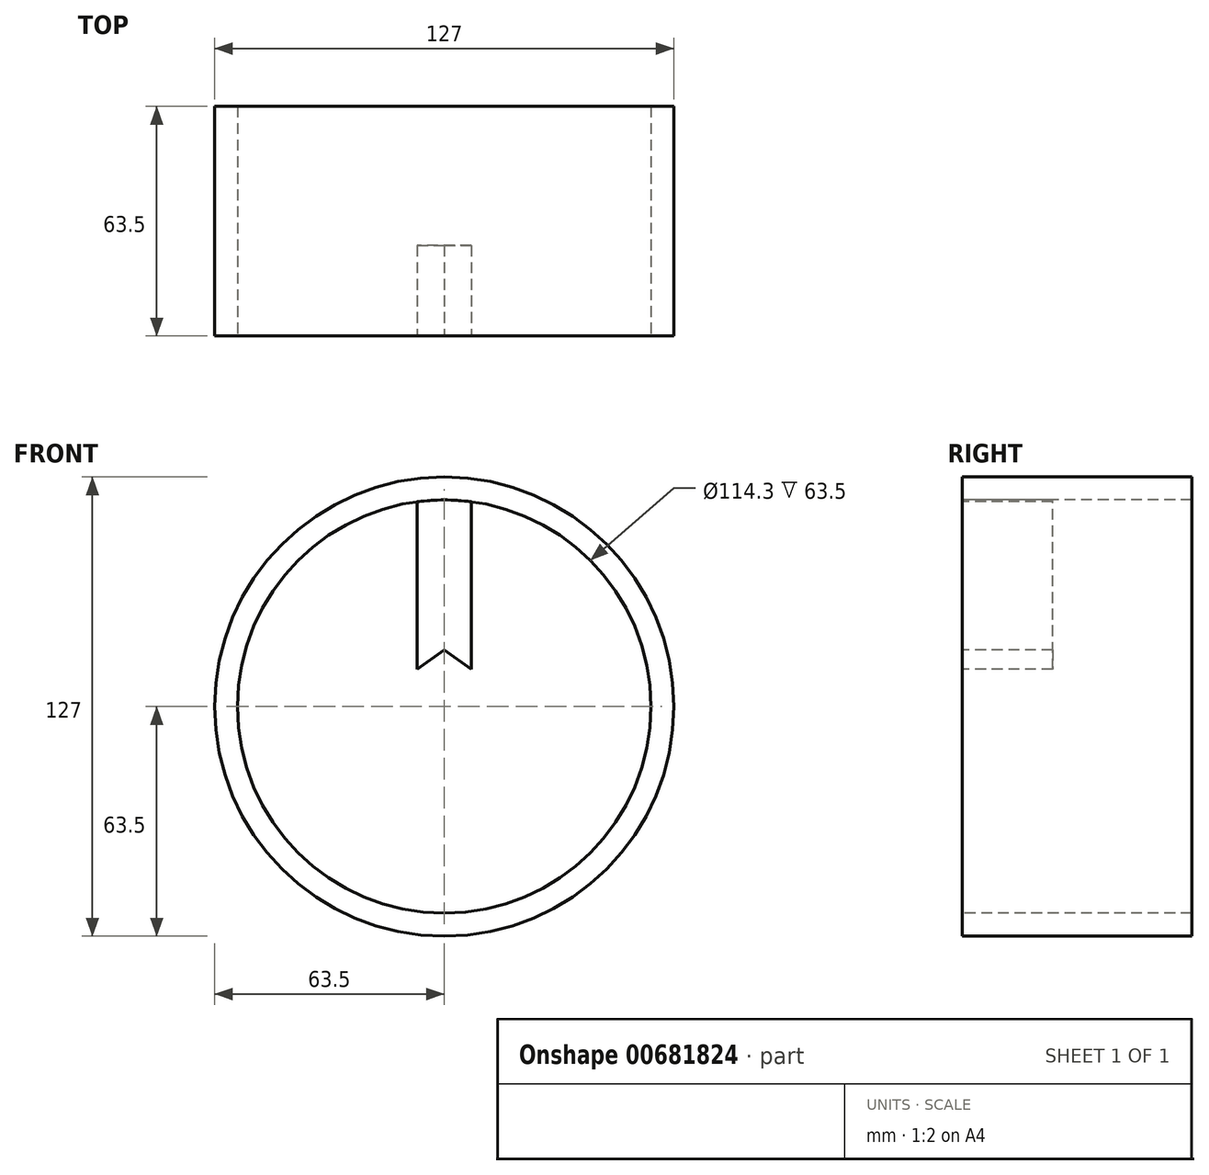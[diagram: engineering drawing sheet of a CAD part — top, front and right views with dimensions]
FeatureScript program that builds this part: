
annotation { "Feature Type Name" : "Feature", "Feature Type Description" : "" }
export const myFeature = defineFeature(function(context is Context, id is Id, definition is map)
    precondition{}
    {
        {
            var Q0;
            Q0=qCreatedBy(makeId("Front.planeOp"),FACE);
            var sketch = newSketch(context, id + "F0", { "sketchPlane" : qUnion([Q0])});
            skCircle(sketch, "E0", {"center": v(0, 0) * mm, "radius": 63.5 * mm});
            skCircle(sketch, "E1", {"center": v(0, 0) * mm, "radius": 57.15 * mm});
            skCircle(sketch, "E2.cCircle", {"center": v(0, 0) * mm, "radius": 46.24 * mm, "construction": true});
            skLineSegment(sketch, "E2.0", {"start": v(54.35, 17.66) * mm, "end": v(33.6, -46.24) * mm});
            skLineSegment(sketch, "E2.1", {"start": v(33.6, -46.24) * mm, "end": v(-33.6, -46.24) * mm});
            skLineSegment(sketch, "E2.2", {"start": v(-33.6, -46.24) * mm, "end": v(-54.35, 17.66) * mm});
            skLineSegment(sketch, "E2.3", {"start": v(-54.35, 17.66) * mm, "end": v(0, 57.15) * mm});
            skLineSegment(sketch, "E2.4", {"start": v(0, 57.15) * mm, "end": v(54.35, 17.66) * mm});
            skPoint(sketch, "E2.0.midPoint", {"position": v(43.97, -14.29) * mm});
            skCircle(sketch, "E3.cCircle", {"center": v(0, 0) * mm, "radius": 12.7 * mm, "construction": true});
            skLineSegment(sketch, "E3.0", {"start": v(-14.93, 4.85) * mm, "end": v(0, 15.7) * mm});
            skLineSegment(sketch, "E3.1", {"start": v(0, 15.7) * mm, "end": v(14.93, 4.85) * mm});
            skLineSegment(sketch, "E3.2", {"start": v(14.93, 4.85) * mm, "end": v(9.23, -12.7) * mm});
            skLineSegment(sketch, "E3.3", {"start": v(9.23, -12.7) * mm, "end": v(-9.23, -12.7) * mm});
            skLineSegment(sketch, "E3.4", {"start": v(-9.23, -12.7) * mm, "end": v(-14.93, 4.85) * mm});
            skPoint(sketch, "E3.0.midPoint", {"position": v(-7.46, 10.27) * mm});
            skLineSegment(sketch, "E4", {"start": v(0, 57.15) * mm, "end": v(0, 15.7) * mm});
            skLineSegment(sketch, "E5", {"start": v(-14.93, 4.85) * mm, "end": v(-54.35, 17.66) * mm});
            skLineSegment(sketch, "E6", {"start": v(-9.23, -12.7) * mm, "end": v(-33.6, -46.24) * mm});
            skLineSegment(sketch, "E7", {"start": v(9.23, -12.7) * mm, "end": v(33.6, -46.24) * mm});
            skLineSegment(sketch, "E8", {"start": v(14.93, 4.85) * mm, "end": v(54.35, 17.66) * mm});
            skLineSegment(sketch, "E9", {"start": v(0, 15.7) * mm, "end": v(7.46, 10.27) * mm});
            skLineSegment(sketch, "E10", {"start": v(-7.46, 10.27) * mm, "end": v(7.46, 10.27) * mm});
            skLineSegment(sketch, "E11", {"start": v(-7.46, 56.66) * mm, "end": v(-7.46, 10.27) * mm});
            skLineSegment(sketch, "E12", {"start": v(7.46, 10.27) * mm, "end": v(7.46, 56.66) * mm});
            skArc(sketch, "E13", {"start": v(7.46, 56.66) * mm, "mid": v(0, 57.15) * mm, "end": v(-7.46, 56.66) * mm});
            skSolve(sketch);
        }
        {
            var Q0;
            Q0=makeQuery(id+"F0.imprint","IMPRINT",FACE,{"disambiguationData":[TD([[makeQuery(id+"F0.imprint","IMPRINT",EDGE,{"derivedFrom":sQuery(id+"F0.wireOp",EDGE,"E0")}),1.0]])]});
            extrude(context, id + "F1", {"entities" : qUnion([Q0]), "oppositeDirection" : true, "depth" : 63.5 * mm, "offsetDistance" : 25.4 * mm});
        }
        {
            var Q0;
            Q0=makeQuery(id+"F0.imprint","IMPRINT",FACE,{"disambiguationData":[TD([[makeQuery(id+"F0.imprint","IMPRINT",EDGE,{"derivedFrom":sQuery(id+"F0.wireOp",EDGE,"E4")}),1.0]])]});
            var Q1;
            {var subQ0=sQuery(id+"F0.wireOp",EDGE,"E4");Q1=makeQuery(id+"F0.imprint","IMPRINT",FACE,{"disambiguationData":[TD([[makeQuery(id+"F0.imprint","IMPRINT",EDGE,{"derivedFrom":subQ0}),-1.0]])]});}
            var Q2;
            {var subQ1=sQuery(id+"F0.wireOp",EDGE,"E1");var subQ3=sQuery(id+"F0.wireOp",EDGE,"E11");var subQ4=makeQuery(id+"F0.imprint","INTERSECT",VERTEX,{"derivedFrom":[subQ1,subQ3]});Q2=makeQuery(id+"F0.imprint","IMPRINT",FACE,{"disambiguationData":[TD([[makeQuery(id+"F0.imprint","IMPRINT",EDGE,{"disambiguationData":[TD([[subQ4,-1.0]])],"derivedFrom":subQ3}),1.0]])]});}
            var Q3;
            {var subQ1=sQuery(id+"F0.wireOp",EDGE,"E1");var subQ3=sQuery(id+"F0.wireOp",EDGE,"E12");var subQ4=makeQuery(id+"F0.imprint","INTERSECT",VERTEX,{"derivedFrom":[subQ1,subQ3]});Q3=makeQuery(id+"F0.imprint","IMPRINT",FACE,{"disambiguationData":[TD([[makeQuery(id+"F0.imprint","IMPRINT",EDGE,{"disambiguationData":[TD([[subQ4,1.0]])],"derivedFrom":subQ3}),1.0]])]});}
            extrude(context, id + "F2", {"entities" : qUnion([Q0, Q1, Q2, Q3]), "oppositeDirection" : true, "depth" : 25 * mm, "offsetDistance" : 25 * mm});
        }
    });
